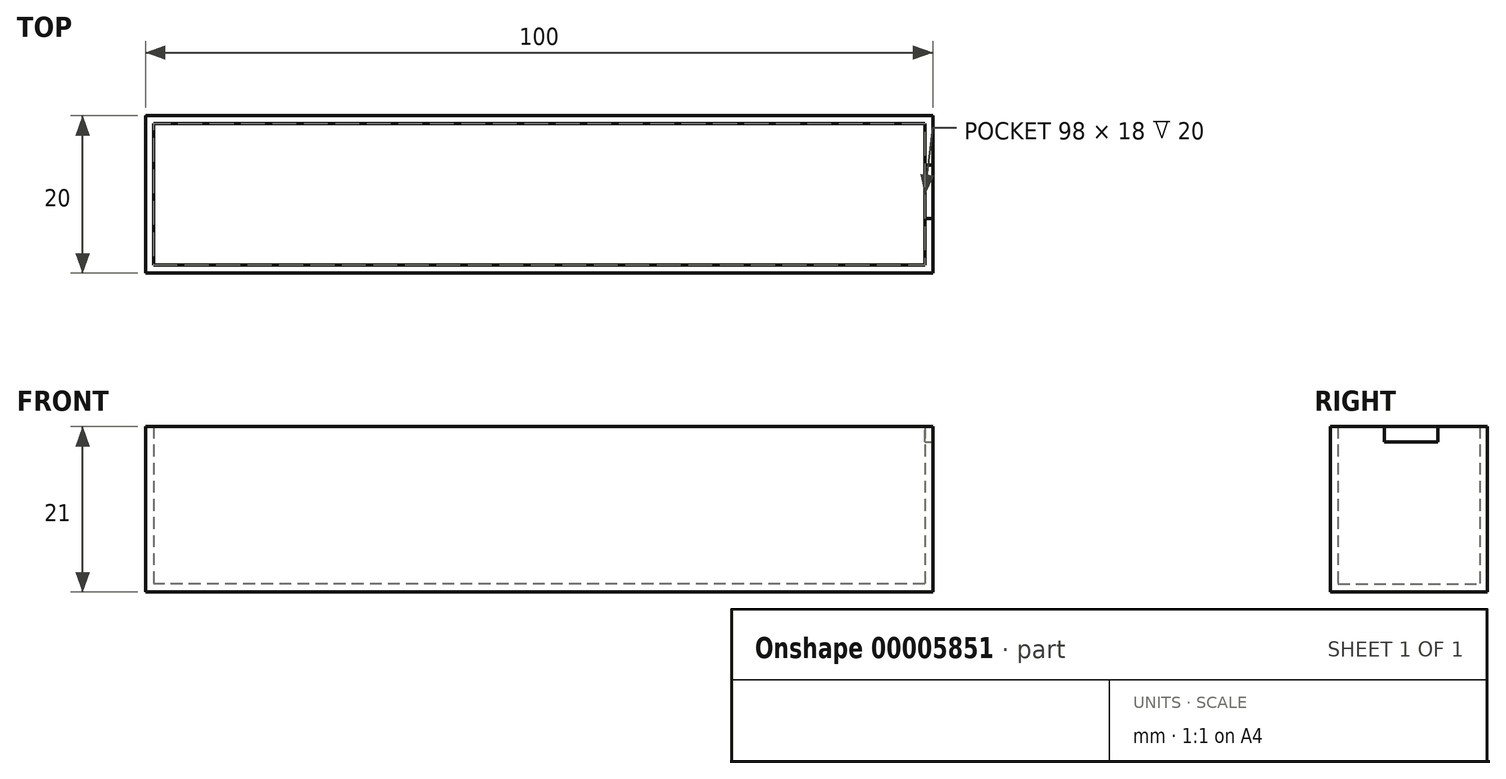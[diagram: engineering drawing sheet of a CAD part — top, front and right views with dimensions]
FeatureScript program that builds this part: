
annotation { "Feature Type Name" : "Feature", "Feature Type Description" : "" }
export const myFeature = defineFeature(function(context is Context, id is Id, definition is map)
    precondition{}
    {
        {
            var Q0;
            Q0=qCreatedBy(makeId("Top.planeOp"),FACE);
            var sketch = newSketch(context, id + "F0", { "sketchPlane" : qUnion([Q0])});
            skLineSegment(sketch, "E0.bottom", {"start": v(-51.34, 26.35) * mm, "end": v(48.66, 26.35) * mm});
            skLineSegment(sketch, "E0.top", {"start": v(-51.34, 6.35) * mm, "end": v(48.66, 6.35) * mm});
            skLineSegment(sketch, "E0.left", {"start": v(-51.34, 26.35) * mm, "end": v(-51.34, 6.35) * mm});
            skLineSegment(sketch, "E0.right", {"start": v(48.66, 26.35) * mm, "end": v(48.66, 6.35) * mm});
            skSolve(sketch);
        }
        {
            var Q0;
            Q0=makeQuery(id+"F0.imprint","IMPRINT",FACE,{"disambiguationData":[TD([[makeQuery(id+"F0.imprint","IMPRINT",EDGE,{"derivedFrom":sQuery(id+"F0.wireOp",EDGE,"E0.bottom")}),-1.0]])]});
            extrude(context, id + "F1", {"entities" : qUnion([Q0]), "depth" : 1 * mm});
        }
        {
            var Q0;
            Q0=makeQuery(id+"F1.opExtrude","CAP_FACE",FACE,{"disambiguationData":[OSD([sQuery(id+"F0.wireOp",EDGE,"E0.bottom"),sQuery(id+"F0.wireOp",EDGE,"E0.top"),sQuery(id+"F0.wireOp",EDGE,"E0.left"),sQuery(id+"F0.wireOp",EDGE,"E0.right")])],"isStart":false});
            var sketch = newSketch(context, id + "F2", { "sketchPlane" : qUnion([Q0])});
            skLineSegment(sketch, "E1.0", {"start": v(47.66, 25.35) * mm, "end": v(-50.34, 25.35) * mm});
            skLineSegment(sketch, "E1.1", {"start": v(47.66, 7.35) * mm, "end": v(47.66, 25.35) * mm});
            skLineSegment(sketch, "E1.2", {"start": v(-50.34, 7.35) * mm, "end": v(47.66, 7.35) * mm});
            skLineSegment(sketch, "E1.3", {"start": v(-50.34, 25.35) * mm, "end": v(-50.34, 7.35) * mm});
            skSolve(sketch);
        }
        {
            var Q0;
            Q0=makeQuery(id+"F2.imprint","IMPRINT",FACE,{"disambiguationData":[TD([[makeQuery(id+"F2.imprint","IMPRINT",EDGE,{"derivedFrom":sQuery(id+"F2.wireOp",EDGE,"E1.0")}),-1.0]])]});
            extrude(context, id + "F3", {"entities" : qUnion([Q0]), "operationType" : NewBodyOperationType.ADD, "depth" : 20 * mm});
        }
        {
            var Q0;
            {var subQ0=sQuery(id+"F0.wireOp",EDGE,"E0.right");Q0=makeQuery(id+"F3.boolean.opBoolean","MERGE",FACE,{"derivedFrom":[makeQuery(id+"F1.opExtrude","SWEPT_FACE",FACE,{"disambiguationData":[OSD([subQ0])]}),makeQuery(id+"F3.opExtrude","SWEPT_FACE",FACE,{"disambiguationData":[OSD([subQ0])]})]});}
            var sketch = newSketch(context, id + "F4", { "sketchPlane" : qUnion([Q0])});
            skLineSegment(sketch, "E2.bottom", {"start": v(13.26, 21.74) * mm, "end": v(20.06, 21.74) * mm});
            skLineSegment(sketch, "E2.top", {"start": v(13.26, 19.04) * mm, "end": v(20.06, 19.04) * mm});
            skLineSegment(sketch, "E2.left", {"start": v(13.26, 21.74) * mm, "end": v(13.26, 19.04) * mm});
            skLineSegment(sketch, "E2.right", {"start": v(20.06, 21.74) * mm, "end": v(20.06, 19.04) * mm});
            skSolve(sketch);
        }
        {
            var Q0;
            {var subQ5=sQuery(id+"F4.wireOp",EDGE,"E2.top");Q0=makeQuery(id+"F4.imprint","IMPRINT",FACE,{"disambiguationData":[TD([[makeQuery(id+"F4.imprint","IMPRINT",EDGE,{"derivedFrom":subQ5}),1.0]])]});}
            extrude(context, id + "F5", {"entities" : qUnion([Q0]), "operationType" : NewBodyOperationType.REMOVE, "oppositeDirection" : true, "depth" : 25 * mm});
        }
    });
